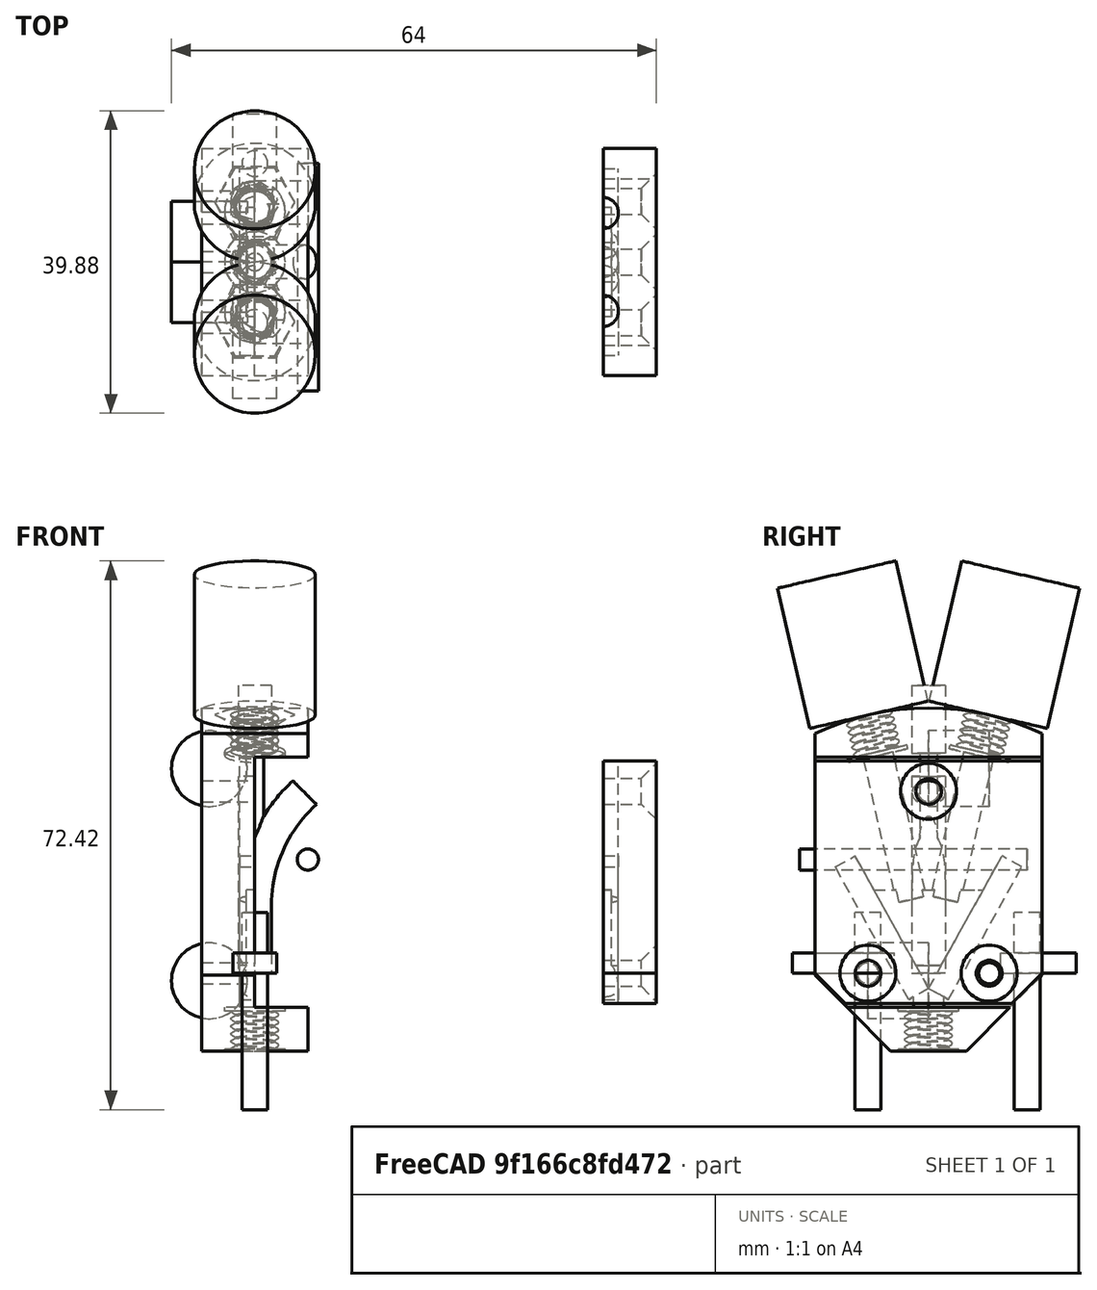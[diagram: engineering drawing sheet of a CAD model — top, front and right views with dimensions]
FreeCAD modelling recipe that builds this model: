
FCSTD DOCUMENT  (FreeCAD 0.17R13528 (Git))
Label: y
License: All rights reserved
LicenseURL: http://en.wikipedia.org/wiki/All_rights_reserved
objects: Part::Cylinder×27, Part::MultiFuse×16, Part::Box×15, Part::Chamfer×7, Part::Cut×6, Part::MultiCommon×4, Part::Feature×3, Part::Mirroring×2, Part::Torus×1, App::DocumentObjectGroup×1
note: 81 computed .brp shape members not serialized (recipe doc carries the construction recipe); baked Part::Feature solids carry a one-line shape summary decoded from their .brp

FEATURE [Part::Cylinder] Cylinder141  label="Cylinder198"
  Angle = 360
  AttacherType = Attacher::AttachEngine3D
  Height = 26
  Placement = pos=(-8,0,-18) rot=(0,0,1;0rad)
  Radius = 1.7
FEATURE [Part::Cylinder] Cylinder142  label="Cylinder199"
  Angle = 360
  AttacherType = Attacher::AttachEngine3D
  Height = 26
  Placement = pos=(13,0,-18) rot=(0,0,1;0rad)
  Radius = 1.7
FEATURE [Part::Box] Box001027045036  label="Cube089"
  AttacherType = Attacher::AttachEngine3D
  Height = 2.7
  Length = 10
  Placement = pos=(9.5,-2.9,0) rot=(0,0,1;0rad)
  Width = 5.8
FEATURE [Part::Box] Box001027045037  label="Cube090"
  AttacherType = Attacher::AttachEngine3D
  Height = 2.7
  Length = 13.5
  Placement = pos=(-18,-2.9,0) rot=(0,0,1;0rad)
  Width = 5.8
FEATURE [Part::MultiFuse] Fusion112050  label="m3-nut-hole-005"
  Shapes = -> [Cylinder141,Box001027045037]
FEATURE [Part::MultiFuse] Fusion112051  label="m3-nut-hole-006"
  Shapes = -> [Box001027045036,Cylinder142]
FEATURE [Part::MultiFuse] Fusion112052  label="m3-nut-holes002"
  Placement = pos=(0,0,0) rot=(0,0,1;1.5708rad)
  Shapes = -> [Fusion112050,Fusion112051]
FEATURE [Part::Cylinder] Cylinder157  label="pneumatic-clearance"
  Angle = 360
  AttacherType = Attacher::AttachEngine3D
  Height = 19
  Placement = pos=(0,7.87329,34.103) rot=(-1,0,0;0.226893rad)
  Radius = 8
FEATURE [Part::Feature] Part__Feature069019  label="M6 thread015"
  Placement = pos=(0,6.74853,29.2311) rot=(-1,0,0;0.226893rad)
  shape: bbox 11.55 x 10.78 x 7.072 mm, 23 faces (baked)
FEATURE [Part::Cylinder] Cylinder161  label="M6-thread-hole"
  Angle = 360
  AttacherType = Attacher::AttachEngine3D
  Height = 6
  Placement = pos=(0,6.63606,28.7439) rot=(-1,0,0;0.226893rad)
  Radius = 4
FEATURE [Part::Cylinder] Cylinder172  label="M3-tap"
  Angle = 360
  AttacherType = Attacher::AttachEngine3D
  Height = 30
  Placement = pos=(7,13,15) rot=(1,0,0;1.5708rad)
  Radius = 1.4
FEATURE [Part::Cylinder] Cylinder188  label="screw-bump-bottom"
  Angle = 360
  AttacherType = Attacher::AttachEngine3D
  Height = 8
  Placement = pos=(-6,8,27) rot=(1,0,0;1.5708rad)
  Radius = 5
FEATURE [Part::Cylinder] Cylinder189  label="screw-bump-top"
  Angle = 360
  AttacherType = Attacher::AttachEngine3D
  Height = 8
  Placement = pos=(-6,0,-1) rot=(1,0,0;1.5708rad)
  Radius = 5
FEATURE [Part::Box] Box001027045132  label="Cube185"
  AttacherType = Attacher::AttachEngine3D
  Height = 18
  Length = 15
  Placement = pos=(-5,-5,-18) rot=(0,0,1;0rad)
  Width = 10
FEATURE [Part::Torus] Torus013
  Angle1 = -180
  Angle2 = 180
  Angle3 = 360
  AttacherType = Attacher::AttachEngine3D
  Placement = pos=(20,0,0) rot=(1,0,0;1.5708rad)
  Radius1 = 20
  Radius2 = 2.2
FEATURE [Part::Box] Box001027045133  label="Cube186"
  AttacherType = Attacher::AttachEngine3D
  Height = 32
  Length = 10
  Placement = pos=(0,-5,-22) rot=(0,0,1;0rad)
  Width = 10
FEATURE [Part::Cylinder] Cylinder190  label="Cylinder237"
  Angle = 360
  AttacherType = Attacher::AttachEngine3D
  Height = 32
  Placement = pos=(0,0,30) rot=(1,0,0;3.14159rad)
  Radius = 1.15
FEATURE [Part::Cylinder] Cylinder191  label="Cylinder238"
  Angle = 360
  AttacherType = Attacher::AttachEngine3D
  Height = 9
  Placement = pos=(0,0,4) rot=(1,0,0;3.14159rad)
  Radius = 2.2
FEATURE [Part::Cylinder] Cylinder192  label="Cylinder239"
  Angle = 360
  AttacherType = Attacher::AttachEngine3D
  Height = 17
  Placement = pos=(0,0,-15) rot=(0,0,1;0rad)
  Radius = 2.2
FEATURE [Part::Cylinder] Cylinder193  label="Cylinder240"
  Angle = 360
  AttacherType = Attacher::AttachEngine3D
  Height = 9
  Placement = pos=(0,0,33) rot=(1,0,0;3.14159rad)
  Radius = 2.2
FEATURE [Part::Box] Box001027045134  label="Cube187"
  AttacherType = Attacher::AttachEngine3D
  Height = 32
  Length = 10
  Placement = pos=(0,-5,-22) rot=(0,0,1;0rad)
  Width = 10
FEATURE [Part::Cut] Cut158
  Base = -> Cylinder192
  Placement = pos=(0,0,6) rot=(1,0,0;3.14159rad)
  Tool = -> Box001027045134
FEATURE [Part::Box] Box001027045135  label="Cube188"
  AttacherType = Attacher::AttachEngine3D
  Height = 25
  Length = 25
  Placement = pos=(-3,-5,-1) rot=(0,0,1;0rad)
  Width = 10
FEATURE [Part::MultiCommon] Common091
  Placement = pos=(5.85786,0,-14.1421) rot=(0,-1,0;0.785398rad)
  Shapes = -> [Torus013,Box001027045135]
FEATURE [Part::MultiCommon] Common089
  Shapes = -> [Common091,Box001027045132]
FEATURE [Part::MultiCommon] Common090
  Placement = pos=(0,0,4) rot=(1,0,0;3.14159rad)
  Shapes = -> [Common089,Box001027045133]
FEATURE [Part::MultiFuse] Fusion112082  label="filament-path001"
  Placement = pos=(0,0,5) rot=(0,0,1;0rad)
  Shapes = -> [Cylinder190,Cut158,Common090,Cylinder191,Cylinder193]
FEATURE [App::DocumentObjectGroup] Group  label="Previous"
  Group = -> [Fusion112052,Cylinder172,Cylinder188,Cylinder189,Fusion112082]
FEATURE [Part::Cylinder] Cylinder
  Angle = 360
  AttacherType = Attacher::AttachEngine3D
  Height = 30
  Placement = pos=(0,2.24951,9.7437) rot=(-1,0,0;0.226893rad)
  Radius = 2
FEATURE [Part::Feature] Part__Feature069020  label="M6 thread016"
  Placement = pos=(0,-6.74853,29.2311) rot=(1,0,0;0.226893rad)
  shape: bbox 11.55 x 10.78 x 7.032 mm, 23 faces (baked)
FEATURE [Part::Cylinder] Cylinder194  label="M6-thread-hole001"
  Angle = 360
  AttacherType = Attacher::AttachEngine3D
  Height = 6
  Placement = pos=(0,-6.63606,28.7439) rot=(1,0,0;0.226893rad)
  Radius = 4
FEATURE [Part::Cylinder] Cylinder195
  Angle = 360
  AttacherType = Attacher::AttachEngine3D
  Height = 30
  Placement = pos=(0,-2.24951,9.7437) rot=(1,0,0;0.226893rad)
  Radius = 2
FEATURE [Part::Cylinder] Cylinder196  label="pneumatic-clearance001"
  Angle = 360
  AttacherType = Attacher::AttachEngine3D
  Height = 19
  Placement = pos=(0,-7.87329,34.103) rot=(1,0,0;0.226893rad)
  Radius = 8
FEATURE [Part::Feature] Part__Feature069021  label="M6 thread017"
  Placement = pos=(0,0,-10) rot=(1,0,0;0rad)
  shape: bbox 11.55 x 10 x 5.798 mm, 23 faces (baked)
FEATURE [Part::Cylinder] Cylinder197  label="M6-thread-hole002"
  Angle = 360
  AttacherType = Attacher::AttachEngine3D
  Height = 6
  Placement = pos=(0,0,-10.5) rot=(1,0,0;0rad)
  Radius = 4
FEATURE [Part::Cylinder] Cylinder198  label="Cylinder241"
  Angle = 360
  AttacherType = Attacher::AttachEngine3D
  Height = 20
  Placement = pos=(0,0,-19) rot=(0,0,1;0rad)
  Radius = 2
FEATURE [Part::Box] Box001027045137  label="Cube190"
  AttacherType = Attacher::AttachEngine3D
  Height = 11
  Length = 2.2
  Placement = pos=(-1.1,-8,0) rot=(0,0,1;0rad)
  Width = 16
FEATURE [Part::Box] Box001027045138  label="Cube191"
  AttacherType = Attacher::AttachEngine3D
  Height = 20
  Length = 4
  Placement = pos=(-2,0,-2) rot=(-1,0,0;0.506145rad)
  Width = 3
FEATURE [Part::Cylinder] Cylinder199  label="M3-tap001"
  Angle = 360
  AttacherType = Attacher::AttachEngine3D
  Height = 30
  Placement = pos=(-15,0,24) rot=(0,1,0;1.5708rad)
  Radius = 1.4
FEATURE [Part::Cylinder] Cylinder200  label="M3-tap002"
  Angle = 360
  AttacherType = Attacher::AttachEngine3D
  Height = 30
  Placement = pos=(-15,-8,0) rot=(0,1,0;1.5708rad)
  Radius = 1.4
FEATURE [Part::Cylinder] Cylinder201  label="M3-tap003"
  Angle = 360
  AttacherType = Attacher::AttachEngine3D
  Height = 30
  Placement = pos=(-15,8,0) rot=(0,1,0;1.5708rad)
  Radius = 1.4
FEATURE [Part::Cylinder] Cylinder202  label="M3-clear-z"
  Angle = 360
  AttacherType = Attacher::AttachEngine3D
  Height = 30
  Placement = pos=(-15,0,24) rot=(0,1,0;1.5708rad)
  Radius = 1.7
FEATURE [Part::Cylinder] Cylinder203  label="M3-clear-a"
  Angle = 360
  AttacherType = Attacher::AttachEngine3D
  Height = 30
  Placement = pos=(-15,8,0) rot=(0,1,0;1.5708rad)
  Radius = 1.7
FEATURE [Part::Cylinder] Cylinder204  label="M3-clear-b"
  Angle = 360
  AttacherType = Attacher::AttachEngine3D
  Height = 30
  Placement = pos=(-15,-8,0) rot=(0,1,0;1.5708rad)
  Radius = 1.7
FEATURE [Part::Cylinder] Cylinder205  label="end-cylinder"
  Angle = 360
  AttacherType = Attacher::AttachEngine3D
  Height = 40
  Placement = pos=(-20,0,0) rot=(0,1,0;1.5708rad)
  Radius = 35
FEATURE [Part::Box] Box  label="Cube"
  AttacherType = Attacher::AttachEngine3D
  Height = 49
  Length = 14
  Placement = pos=(-7,-15,-10.25) rot=(0,0,1;0rad)
  Width = 30
FEATURE [Part::MultiCommon] Common
  Shapes = -> [Box,Cylinder205]
FEATURE [Part::Chamfer] Chamfer003  label="base-a"
  Base = -> Common
  Edges = 2 edges r=10: [Edge7,Edge11]
FEATURE [Part::Box] Box001027045139  label="top-slot"
  AttacherType = Attacher::AttachEngine3D
  Height = 33
  Length = 14
  Placement = pos=(0,-17,-4.5) rot=(0,0,1;0rad)
  Width = 34
FEATURE [Part::Box] Box001027045140  label="top-slot001"
  AttacherType = Attacher::AttachEngine3D
  Height = 32
  Length = 7
  Placement = pos=(0,-15,-4) rot=(0,0,1;0rad)
  Width = 30
FEATURE [Part::Chamfer] Chamfer004  label="top-a"
  Base = -> Box001027045140
  Edges = 2 edges r=4: [Edge9,Edge11]
FEATURE [Part::MultiFuse] Fusion112083  label="M3-clears"
  Shapes = -> [Cylinder202,Cylinder203,Cylinder204]
FEATURE [Part::MultiFuse] Fusion112084  label="M3-taps"
  Shapes = -> [Cylinder199,Cylinder200,Cylinder201]
FEATURE [Part::MultiFuse] Fusion112088  label="threads"
  Shapes = -> [Part__Feature069021,Part__Feature069020,Part__Feature069019]
FEATURE [Part::MultiFuse] Fusion112092  label="M6-holes"
  Shapes = -> [Cylinder161,Cylinder194,Cylinder197]
FEATURE [Part::Chamfer] Chamfer
  Base = -> Box001027045137
  Edges = 2 edges r=7: [Edge9,Edge11]
FEATURE [Part::Chamfer] Chamfer009
  Base = -> Chamfer
  Edges = 2 edges r=3: [Edge8,Edge17]
FEATURE [Part::MultiFuse] Fusion112093  label="Y"
  Shapes = -> [Chamfer009,Cylinder195,Cylinder,Cylinder198]
FEATURE [Part::Cylinder] Cylinder209
  Angle = 360
  AttacherType = Attacher::AttachEngine3D
  Height = 30
  Placement = pos=(0,2.24951,9.7437) rot=(-1,0,0;0.226893rad)
  Radius = 2
FEATURE [Part::Cylinder] Cylinder210
  Angle = 360
  AttacherType = Attacher::AttachEngine3D
  Height = 30
  Placement = pos=(0,-2.24951,9.7437) rot=(1,0,0;0.226893rad)
  Radius = 2
FEATURE [Part::Cylinder] Cylinder211  label="Cylinder243"
  Angle = 360
  AttacherType = Attacher::AttachEngine3D
  Height = 20
  Placement = pos=(0,0,-19) rot=(0,0,1;0rad)
  Radius = 2
FEATURE [Part::Box] Box001027045145  label="Cube196"
  AttacherType = Attacher::AttachEngine3D
  Height = 11
  Length = 2.2
  Placement = pos=(-1.1,-8,0) rot=(0,0,1;0rad)
  Width = 16
FEATURE [Part::Chamfer] Chamfer010
  Base = -> Box001027045145
  Edges = 2 edges r=7: [Edge9,Edge11]
FEATURE [Part::Chamfer] Chamfer011
  Base = -> Chamfer010
  Edges = 2 edges r=3: [Edge8,Edge17]
FEATURE [Part::MultiFuse] Fusion112094  label="Y002"
  Shapes = -> [Chamfer011,Cylinder210,Cylinder209,Cylinder211]
FEATURE [Part::MultiFuse] Fusion112095  label="Y-M6-holes"
  Shapes = -> [Fusion112093,Fusion112092]
FEATURE [Part::MultiFuse] Fusion112096  label="Y-M6-M3"
  Shapes = -> [Fusion112095,Fusion112084]
FEATURE [Part::Cut] Cut  label="base-a001"
  Base = -> Chamfer003
  Tool = -> Fusion112096
FEATURE [Part::MultiFuse] Fusion112098  label="base-b"
  Shapes = -> [Cut,Fusion112088]
FEATURE [Part::Cut] Cut160  label="base-c"
  Base = -> Fusion112098
  Tool = -> Box001027045139
FEATURE [Part::Box] Box001027045146  label="Cube197"
  AttacherType = Attacher::AttachEngine3D
  Height = 20
  Length = 4
  Placement = pos=(-2,0,-2) rot=(-1,0,0;0.506145rad)
  Width = 3
FEATURE [Part::Mirroring] Part__Mirroring  label="Cube197 (Mirror #2)"
  Base = (0,0,0)
  Normal = (0,1,0)
  Source = -> Box001027045146
FEATURE [Part::MultiFuse] Fusion  label="split-holders"
  Shapes = -> [Box001027045138,Part__Mirroring]
FEATURE [Part::Box] Box001027045147  label="Cube198"
  AttacherType = Attacher::AttachEngine3D
  Height = 20
  Length = 4
  Placement = pos=(-2,0,-2) rot=(-1,0,0;0.506145rad)
  Width = 3
FEATURE [Part::Box] Box001027045148  label="Cube199"
  AttacherType = Attacher::AttachEngine3D
  Height = 20
  Length = 4
  Placement = pos=(-2,0,-2) rot=(-1,0,0;0.506145rad)
  Width = 3
FEATURE [Part::Mirroring] Part__Mirroring002  label="Cube197 (Mirror #2)001"
  Base = (0,0,0)
  Normal = (0,1,0)
  Source = -> Box001027045148
FEATURE [Part::MultiFuse] Fusion112099  label="split-holders001"
  Shapes = -> [Box001027045147,Part__Mirroring002]
FEATURE [Part::Cut] Cut161  label="base"
  Base = -> Cut160
  Tool = -> Fusion
FEATURE [Part::MultiFuse] Fusion112100  label="y-top-M3"
  Shapes = -> [Fusion112094,Fusion112083]
FEATURE [Part::Cut] Cut162  label="top-b"
  Base = -> Chamfer004
  Tool = -> Fusion112100
FEATURE [Part::Cut] Cut163  label="top-d"
  Base = -> Cut162
  Tool = -> Fusion112099
FEATURE [Part::Chamfer] Chamfer012  label="top"
  Base = -> Cut163
  Edges = 3 edges r=2: [Edge49,Edge53,Edge54]
  Placement = pos=(46,0,0) rot=(0,0,1;0rad)
